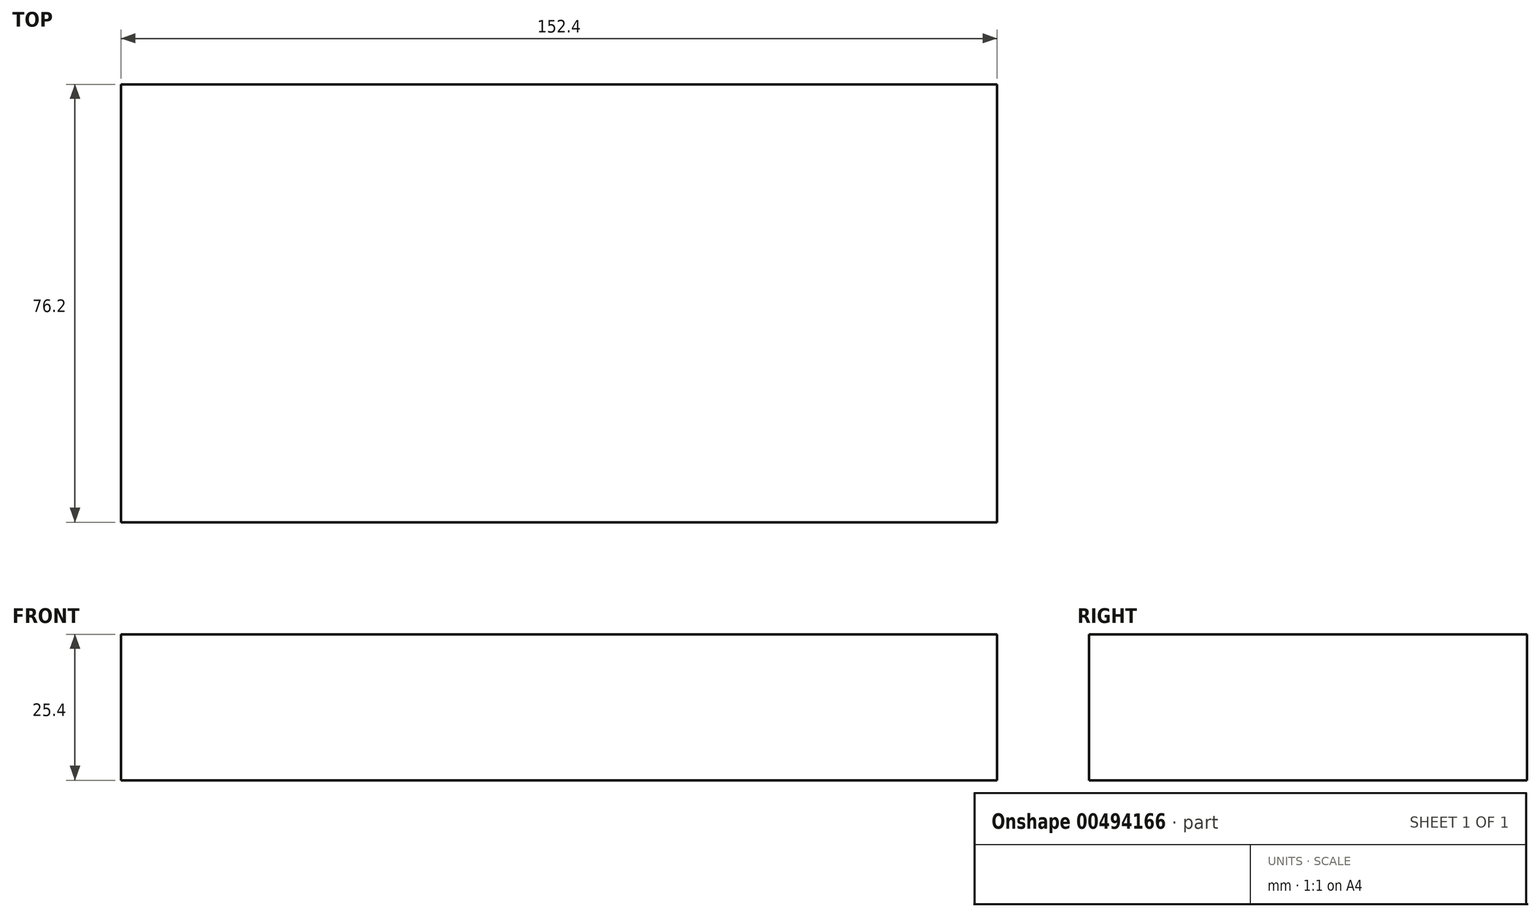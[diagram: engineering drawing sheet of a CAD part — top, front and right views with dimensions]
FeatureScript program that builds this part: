
annotation { "Feature Type Name" : "Feature", "Feature Type Description" : "" }
export const myFeature = defineFeature(function(context is Context, id is Id, definition is map)
    precondition{}
    {
        {
            var Q0;
            Q0=qCreatedBy(makeId("Top.planeOp"),FACE);
            var sketch = newSketch(context, id + "F0", { "sketchPlane" : qUnion([Q0])});
            skLineSegment(sketch, "E0.bottom", {"start": v(-76.94, 63.8) * mm, "end": v(75.46, 63.8) * mm});
            skLineSegment(sketch, "E0.top", {"start": v(-76.94, -12.4) * mm, "end": v(75.46, -12.4) * mm});
            skLineSegment(sketch, "E0.left", {"start": v(-76.94, 63.8) * mm, "end": v(-76.94, -12.4) * mm});
            skLineSegment(sketch, "E0.right", {"start": v(75.46, 63.8) * mm, "end": v(75.46, -12.4) * mm});
            skLineSegment(sketch, "E1.bottom", {"start": v(24.66, 13) * mm, "end": v(75.46, 13) * mm});
            skLineSegment(sketch, "E1.top", {"start": v(24.66, -12.4) * mm, "end": v(75.46, -12.4) * mm});
            skLineSegment(sketch, "E1.left", {"start": v(24.66, 13) * mm, "end": v(24.66, -12.4) * mm});
            skLineSegment(sketch, "E1.right", {"start": v(75.46, 13) * mm, "end": v(75.46, -12.4) * mm});
            skSolve(sketch);
        }
        {
            var Q0;
            Q0 = qSketchRegion(id + "F0", true);
            extrude(context, id + "F1", {"entities" : qUnion([Q0]), "depth" : 25.4 * mm});
        }
    });
